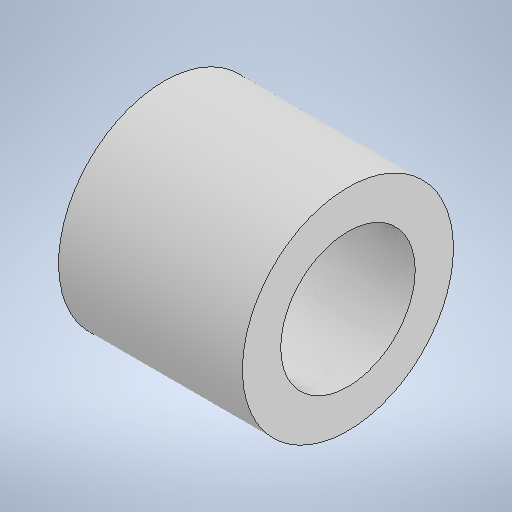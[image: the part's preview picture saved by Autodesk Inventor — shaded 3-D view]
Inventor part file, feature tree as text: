
AUTODESK INVENTOR PART (.ipt)
format: ipt  version: 2025.1 (Build 291241020, 241B)  size: 226,304 bytes
history: native  units: in
note: dims shown in document units (in); Inventor stores cm internally (conversion verified against a paired STEP export)
features: extrude x2, sketch x2, projected_geometry x1
ambient origin geometry x8: Origin, YZ Plane, XZ Plane, XY Plane, X Axis, Y Axis, Z Axis, Center Point
bodies: Solid1 (feature_tree)
feature tree (5):
  extrude  "Extrusion1"  Depth=0.8in
  extrude  "Extrusion2"  Depth=0.08in TaperAngle=0.0deg
  sketch  "Sketch1"  dims[d0=0.51in d1=0.8in]
  sketch  "Sketch2"  dims[d2=0.6174in d3=0.0in d4=0.08in d5=0.0in]
  projected_geometry  "Projected Loop1"
